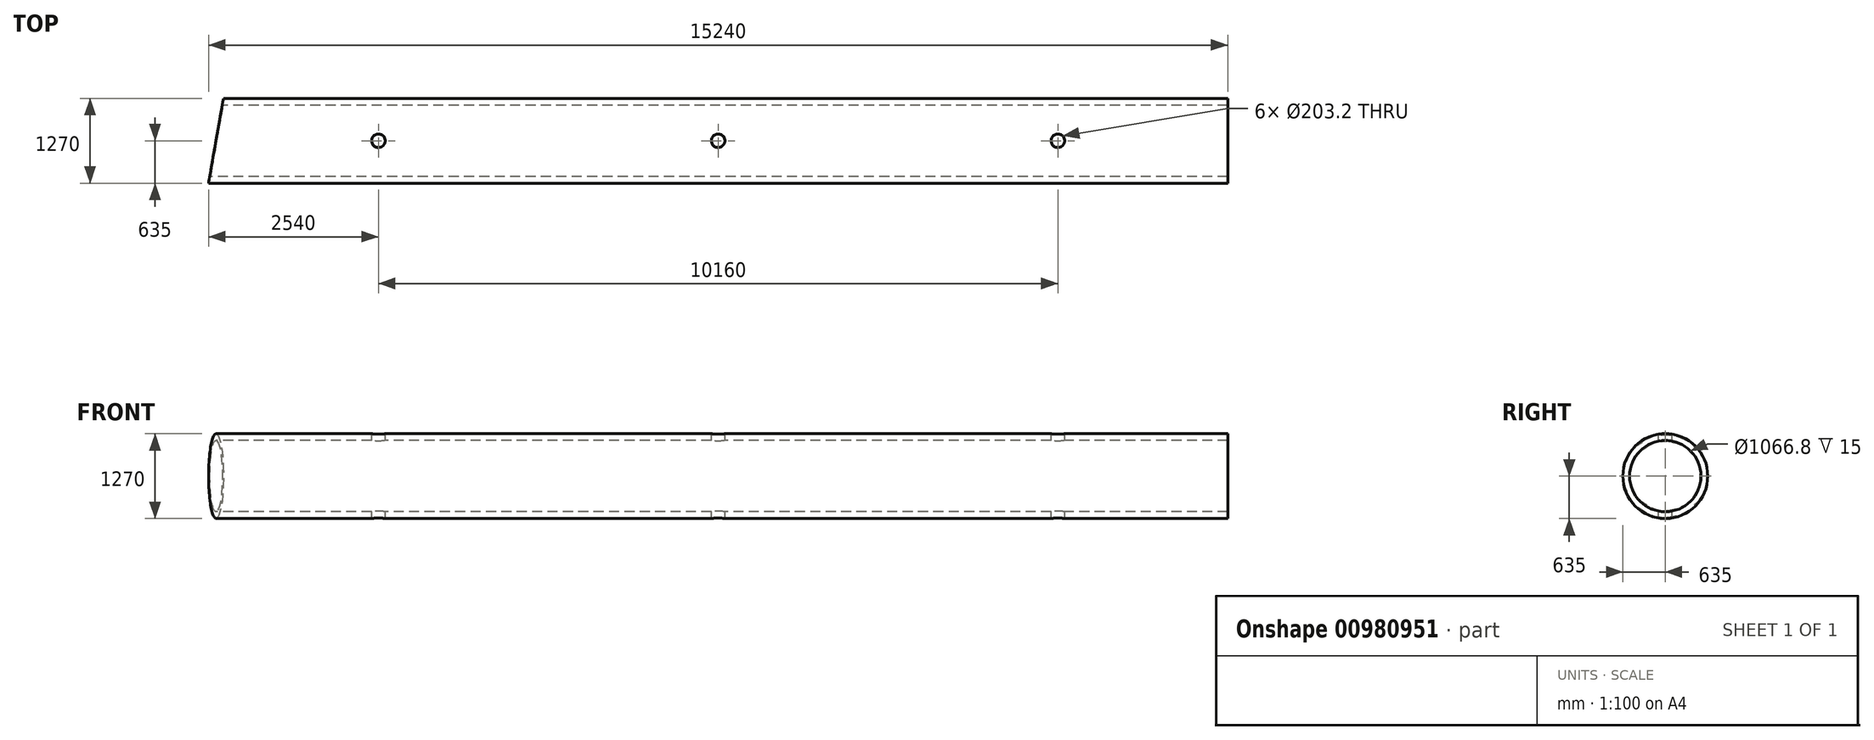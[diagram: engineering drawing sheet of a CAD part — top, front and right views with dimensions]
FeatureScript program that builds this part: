
annotation { "Feature Type Name" : "Feature", "Feature Type Description" : "" }
export const myFeature = defineFeature(function(context is Context, id is Id, definition is map)
    precondition{}
    {
        {
            var Q0;
            Q0=qCreatedBy(makeId("Right.planeOp"),FACE);
            var sketch = newSketch(context, id + "F0", { "sketchPlane" : qUnion([Q0])});
            skCircle(sketch, "E0", {"center": v(0, 0) * mm, "radius": 635 * mm});
            skCircle(sketch, "E1", {"center": v(0, 0) * mm, "radius": 533.4 * mm});
            skSolve(sketch);
        }
        {
            var Q0;
            Q0 = qSketchRegion(id + "F0", true);
            extrude(context, id + "F1", {"entities" : qUnion([Q0]), "depth" : 15240 * mm, "offsetDistance" : 25.4 * mm});
        }
        {
            var Q0;
            Q0=qCreatedBy(makeId("Top.planeOp"),FACE);
            var sketch = newSketch(context, id + "F2", { "sketchPlane" : qUnion([Q0])});
            skCircle(sketch, "E2", {"center": v(2540, 0) * mm, "radius": 101.6 * mm});
            skCircle(sketch, "E3", {"center": v(7620, 0) * mm, "radius": 101.6 * mm});
            skCircle(sketch, "E4", {"center": v(12700, 0) * mm, "radius": 101.6 * mm});
            skSolve(sketch);
        }
        {
            var Q0;
            Q0 = qSketchRegion(id + "F2", true);
            extrude(context, id + "F3", {"entities" : qUnion([Q0]), "operationType" : NewBodyOperationType.REMOVE, "endBound" : BoundingType.SYMMETRIC, "oppositeDirection" : true, "depth" : 1524 * mm, "offsetDistance" : 25.4 * mm});
        }
        {
            var Q0;
            Q0=qCreatedBy(makeId("Top.planeOp"),FACE);
            var sketch = newSketch(context, id + "F4", { "sketchPlane" : qUnion([Q0])});
            skLineSegment(sketch, "E5", {"start": v(0, 0) * mm, "end": v(0, -635) * mm});
            skLineSegment(sketch, "E6", {"start": v(0, -635) * mm, "end": v(303.91, 1088.58) * mm});
            skLineSegment(sketch, "E7", {"start": v(303.91, 1088.58) * mm, "end": v(0, 1088.58) * mm});
            skLineSegment(sketch, "E8", {"start": v(0, 1088.58) * mm, "end": v(0, 0) * mm});
            skSolve(sketch);
        }
        {
            var Q0;
            Q0 = qSketchRegion(id + "F4", true);
            extrude(context, id + "F5", {"entities" : qUnion([Q0]), "operationType" : NewBodyOperationType.REMOVE, "endBound" : BoundingType.SYMMETRIC, "depth" : 1524 * mm, "offsetDistance" : 25.4 * mm});
        }
    });
